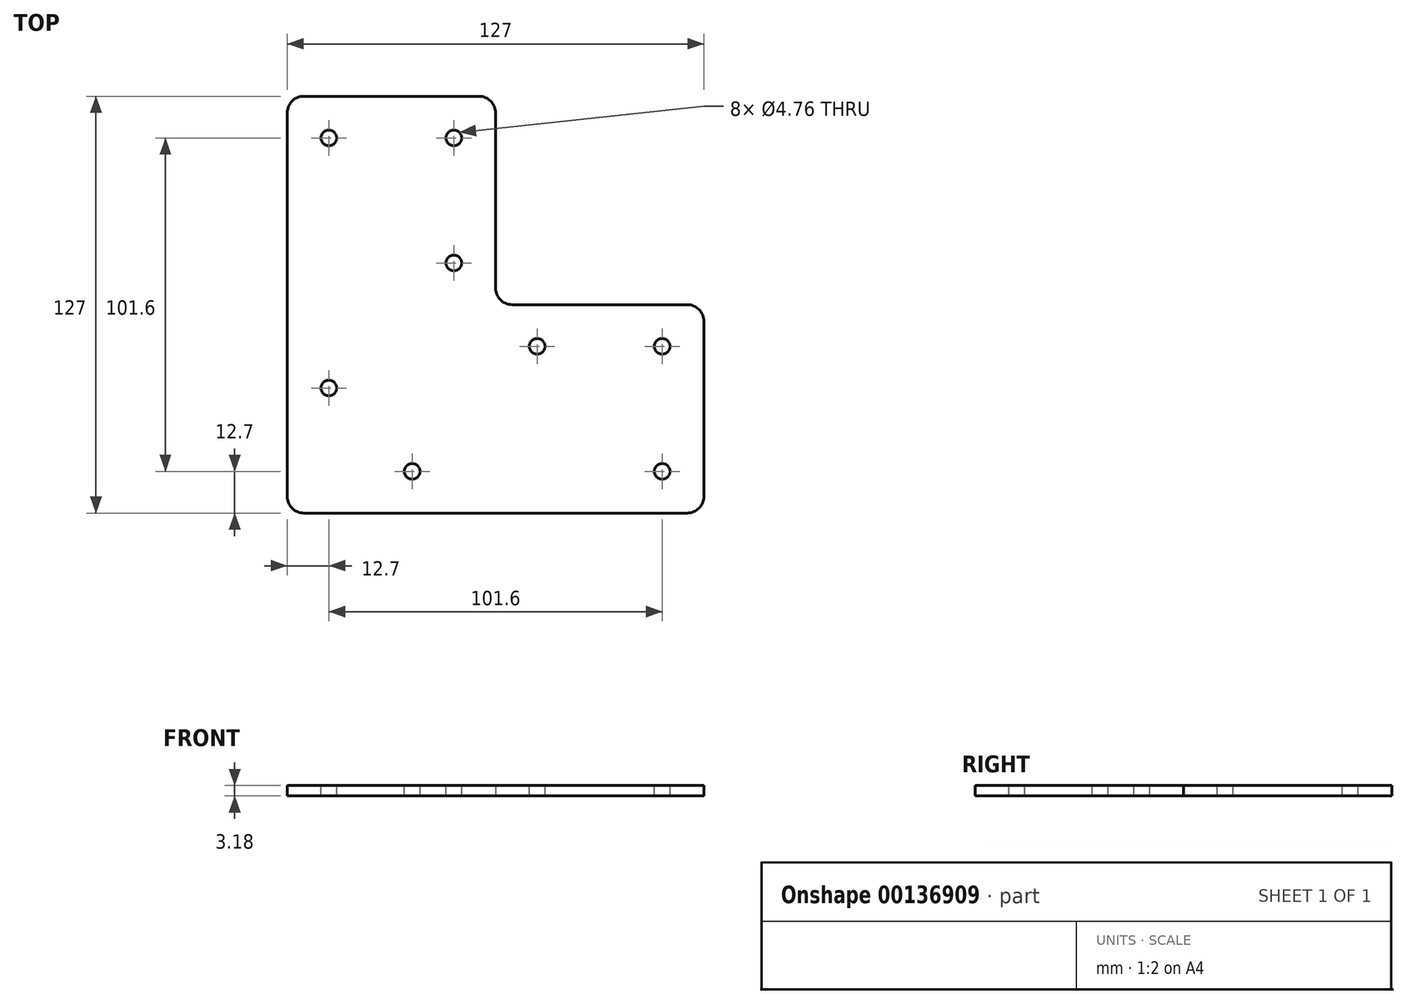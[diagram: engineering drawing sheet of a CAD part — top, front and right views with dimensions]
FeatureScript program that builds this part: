
annotation { "Feature Type Name" : "Feature", "Feature Type Description" : "" }
export const myFeature = defineFeature(function(context is Context, id is Id, definition is map)
    precondition{}
    {
        {
            var Q0;
            Q0=qCreatedBy(makeId("Top.planeOp"),FACE);
            var sketch = newSketch(context, id + "F0", { "sketchPlane" : qUnion([Q0])});
            skLineSegment(sketch, "E0", {"start": v(0, 0) * mm, "end": v(0, -127) * mm});
            skLineSegment(sketch, "E1", {"start": v(0, -127) * mm, "end": v(127, -127) * mm});
            skLineSegment(sketch, "E2", {"start": v(127, -127) * mm, "end": v(127, -63.5) * mm});
            skLineSegment(sketch, "E3", {"start": v(127, -63.5) * mm, "end": v(63.5, -63.5) * mm});
            skLineSegment(sketch, "E4", {"start": v(63.5, -63.5) * mm, "end": v(63.5, 0) * mm});
            skLineSegment(sketch, "E5", {"start": v(63.5, 0) * mm, "end": v(0, 0) * mm});
            skSolve(sketch);
        }
        {
            var Q0;
            Q0=makeQuery(id+"F0.imprint","IMPRINT",FACE,{"disambiguationData":[TD([[makeQuery(id+"F0.imprint","IMPRINT",EDGE,{"derivedFrom":sQuery(id+"F0.wireOp",EDGE,"E0")}),1.0]])]});
            extrude(context, id + "F1", {"entities" : qUnion([Q0]), "depth" : 3.17 * mm});
        }
        {
            var Q0;
            Q0=makeQuery(id+"F1.opExtrude","CAP_FACE",FACE,{"disambiguationData":[OSD([sQuery(id+"F0.wireOp",EDGE,"E0"),sQuery(id+"F0.wireOp",EDGE,"E1"),sQuery(id+"F0.wireOp",EDGE,"E2"),sQuery(id+"F0.wireOp",EDGE,"E3"),sQuery(id+"F0.wireOp",EDGE,"E4"),sQuery(id+"F0.wireOp",EDGE,"E5")])],"isStart":false});
            var sketch = newSketch(context, id + "F2", { "sketchPlane" : qUnion([Q0])});
            skPoint(sketch, "E6", {"position": v(114.3, -114.3) * mm});
            skPoint(sketch, "E7", {"position": v(114.3, -76.2) * mm});
            skPoint(sketch, "E8", {"position": v(76.2, -76.2) * mm});
            skPoint(sketch, "E9", {"position": v(38.1, -114.3) * mm});
            skPoint(sketch, "E10", {"position": v(12.7, -88.9) * mm});
            skPoint(sketch, "E11", {"position": v(50.8, -50.8) * mm});
            skPoint(sketch, "E12", {"position": v(50.8, -12.7) * mm});
            skPoint(sketch, "E13", {"position": v(12.7, -12.7) * mm});
            skSolve(sketch);
        }
        {
            var Q0;
            Q0=sQuery(id+"F2.wireOp",VERTEX,"E13");
            var Q1;
            Q1=sQuery(id+"F2.wireOp",VERTEX,"E12");
            var Q2;
            Q2=sQuery(id+"F2.wireOp",VERTEX,"E11");
            var Q3;
            Q3=sQuery(id+"F2.wireOp",VERTEX,"E10");
            var Q4;
            Q4=sQuery(id+"F2.wireOp",VERTEX,"E9");
            var Q5;
            Q5=sQuery(id+"F2.wireOp",VERTEX,"E8");
            var Q6;
            Q6=sQuery(id+"F2.wireOp",VERTEX,"E7");
            var Q7;
            Q7=sQuery(id+"F2.wireOp",VERTEX,"E6");
            var Q8;
            Q8=makeQuery(id+"F1.opExtrude","SWEPT_BODY",BODY,{"disambiguationData":[OSD([sQuery(id+"F0.wireOp",EDGE,"E0"),sQuery(id+"F0.wireOp",EDGE,"E1"),sQuery(id+"F0.wireOp",EDGE,"E2"),sQuery(id+"F0.wireOp",EDGE,"E3"),sQuery(id+"F0.wireOp",EDGE,"E4"),sQuery(id+"F0.wireOp",EDGE,"E5")])]});
            hole(context, id + "F3", {"style" : HoleStyle.SIMPLE, "endStyle" : HoleEndStyle.THROUGH, "holeDiameter" : 4.76 * mm, "startFromSketch" : true, "locations" : qUnion([Q0, Q1, Q2, Q3, Q4, Q5, Q6, Q7]), "scope" : qUnion([Q8]), "isTappedThrough" : true});
        }
        {
            var Q0;
            Q0=makeQuery(id+"F1.opExtrude","SWEPT_EDGE",EDGE,{"disambiguationData":[OSD([sQuery(id+"F0.wireOp",EDGE,"E3"),sQuery(id+"F0.wireOp",EDGE,"E4")])]});
            var Q1;
            Q1=makeQuery(id+"F1.opExtrude","SWEPT_EDGE",EDGE,{"disambiguationData":[OSD([sQuery(id+"F0.wireOp",EDGE,"E4"),sQuery(id+"F0.wireOp",EDGE,"E5")])]});
            var Q2;
            Q2=makeQuery(id+"F1.opExtrude","SWEPT_EDGE",EDGE,{"disambiguationData":[OSD([sQuery(id+"F0.wireOp",EDGE,"E0"),sQuery(id+"F0.wireOp",EDGE,"E5")])]});
            var Q3;
            Q3=makeQuery(id+"F1.opExtrude","SWEPT_EDGE",EDGE,{"disambiguationData":[OSD([sQuery(id+"F0.wireOp",EDGE,"E2"),sQuery(id+"F0.wireOp",EDGE,"E3")])]});
            var Q4;
            Q4=makeQuery(id+"F1.opExtrude","SWEPT_EDGE",EDGE,{"disambiguationData":[OSD([sQuery(id+"F0.wireOp",EDGE,"E1"),sQuery(id+"F0.wireOp",EDGE,"E2")])]});
            var Q5;
            Q5=makeQuery(id+"F1.opExtrude","SWEPT_EDGE",EDGE,{"disambiguationData":[OSD([sQuery(id+"F0.wireOp",EDGE,"E0"),sQuery(id+"F0.wireOp",EDGE,"E1")])]});
            fillet(context, id + "F4", {"entities" : qUnion([Q0, Q1, Q2, Q3, Q4, Q5]), "radius" : 5.08 * mm, "tangentPropagation" : true, "allowEdgeOverflow" : false});
        }
    });
